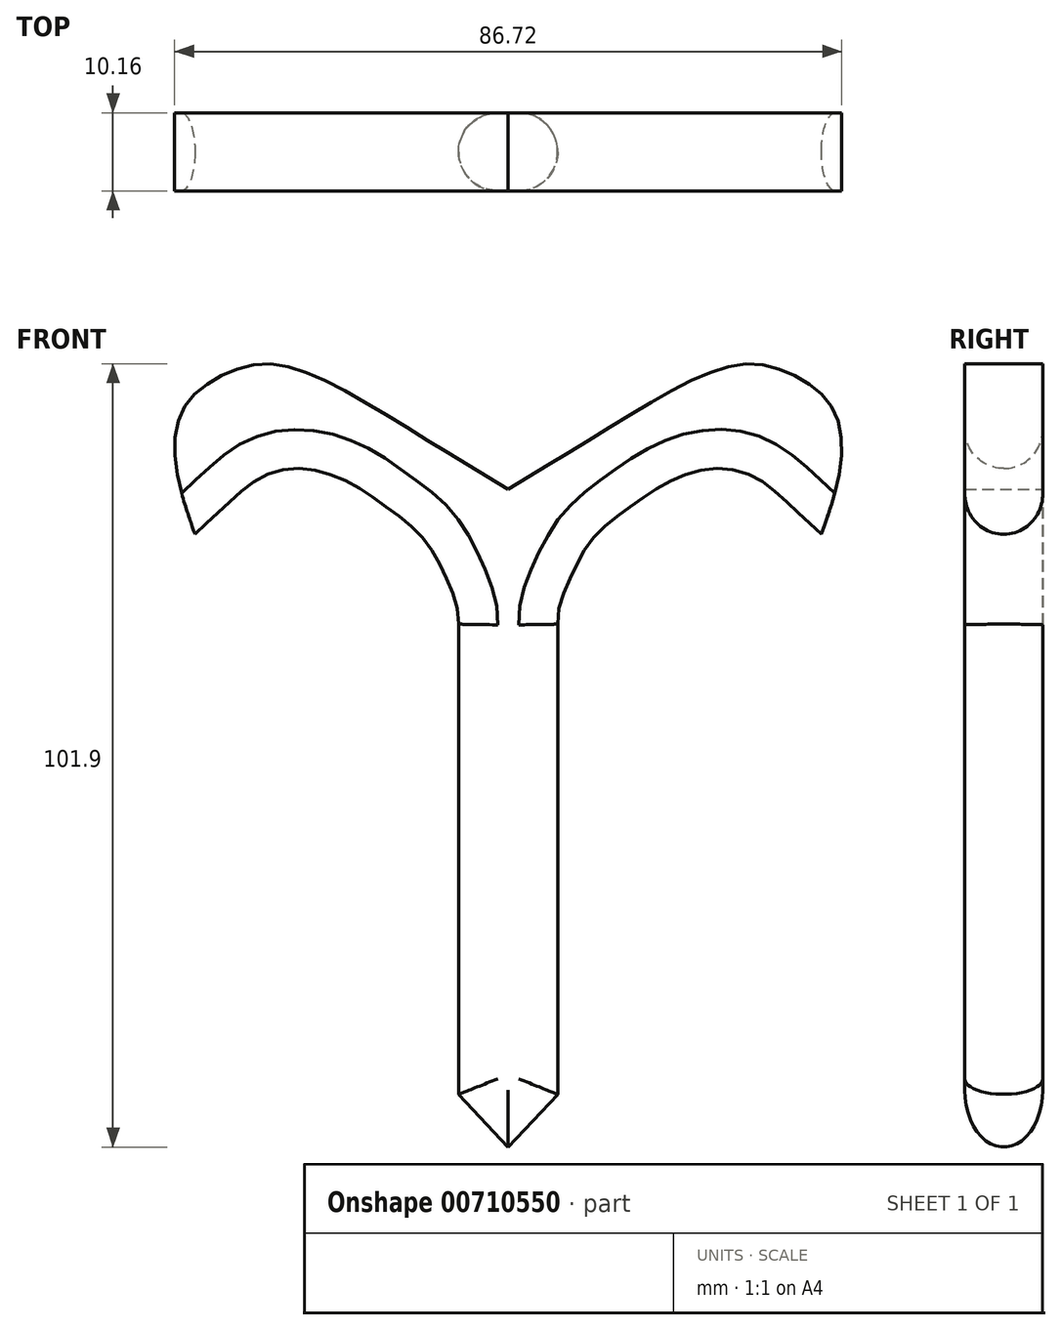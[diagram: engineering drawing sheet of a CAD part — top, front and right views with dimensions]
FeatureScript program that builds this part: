
annotation { "Feature Type Name" : "Feature", "Feature Type Description" : "" }
export const myFeature = defineFeature(function(context is Context, id is Id, definition is map)
    precondition{}
    {
        {
            var Q0;
            Q0=qCreatedBy(makeId("Front.planeOp"),FACE);
            var sketch = newSketch(context, id + "F0", { "sketchPlane" : qUnion([Q0])});
            skFitSpline(sketch, "E0", {"points": [v(-40.72, -3.3) * mm, v(-36.06, 1.06) * mm, v(-31.4, 4.47) * mm, v(-25.7, 5.13) * mm, v(-20, 3.06) * mm, v(-15.49, 0) * mm, v(-11.42, -3.38) * mm, v(-8.6, -7.82) * mm, v(-6.6, -12.85) * mm, v(-6.46, -15) * mm], "startDerivative": vector(37.94, 35.86) * mm, "endDerivative": vector(-0.94, -26.86) * mm});
            skLineSegment(sketch, "E1", {"start": v(-6.46, -15) * mm, "end": v(-6.46, -76.17) * mm});
            skLineSegment(sketch, "E2", {"start": v(-6.46, -76.17) * mm, "end": v(0, -83.02) * mm});
            skFitSpline(sketch, "E3", {"points": [v(-40.72, -3.3) * mm, v(-43.2, 5.6) * mm, v(-42.39, 12.7) * mm, v(-38.07, 16.9) * mm, v(-31.55, 18.88) * mm, v(-23.28, 16.43) * mm, v(-11.51, 9.56) * mm, v(0, 2.57) * mm], "startDerivative": vector(-21.78, 62.02) * mm, "endDerivative": vector(65.3, -39.32) * mm});
            skLineSegment(sketch, "E4", {"start": v(0, -5.7) * mm, "end": v(0, -12.11) * mm});
            skFitSpline(sketch, "E5.MirrorCS", {"points": [v(40.72, -3.3) * mm, v(43.2, 5.6) * mm, v(42.39, 12.7) * mm, v(38.07, 16.9) * mm, v(31.55, 18.88) * mm, v(23.28, 16.43) * mm, v(11.51, 9.56) * mm, v(0, 2.57) * mm], "startDerivative": vector(21.78, 62.02) * mm, "endDerivative": vector(-65.3, -39.32) * mm});
            skFitSpline(sketch, "E6.MirrorCS", {"points": [v(40.72, -3.3) * mm, v(36.06, 1.06) * mm, v(31.4, 4.47) * mm, v(25.7, 5.13) * mm, v(20, 3.06) * mm, v(15.49, 0) * mm, v(11.42, -3.38) * mm, v(8.6, -7.82) * mm, v(6.6, -12.85) * mm, v(6.46, -15) * mm], "startDerivative": vector(-37.94, 35.86) * mm, "endDerivative": vector(0.94, -26.86) * mm});
            skLineSegment(sketch, "E7.MirrorCS", {"start": v(6.46, -15) * mm, "end": v(6.46, -76.17) * mm});
            skLineSegment(sketch, "E8.MirrorCS", {"start": v(6.46, -76.17) * mm, "end": v(0, -83.02) * mm});
            skSolve(sketch);
        }
        {
            var Q0;
            Q0=makeQuery(id+"F0.imprint","IMPRINT",FACE,{"disambiguationData":[TD([[makeQuery(id+"F0.imprint","IMPRINT",EDGE,{"derivedFrom":sQuery(id+"F0.wireOp",EDGE,"E0")}),1.0]])]});
            extrude(context, id + "F1", {"entities" : qUnion([Q0]), "depth" : 5.08 * mm, "offsetDistance" : 25.4 * mm});
        }
        {
            var Q0;
            Q0=makeQuery(id+"F1.opExtrude","CAP_FACE",FACE,{"disambiguationData":[OSD([sQuery(id+"F0.wireOp",EDGE,"E0"),sQuery(id+"F0.wireOp",EDGE,"E1"),sQuery(id+"F0.wireOp",EDGE,"E2"),sQuery(id+"F0.wireOp",EDGE,"E3"),sQuery(id+"F0.wireOp",EDGE,"E5.MirrorCS"),sQuery(id+"F0.wireOp",EDGE,"E6.MirrorCS"),sQuery(id+"F0.wireOp",EDGE,"E7.MirrorCS"),sQuery(id+"F0.wireOp",EDGE,"E8.MirrorCS")])],"isStart":true});
            extrude(context, id + "F2", {"entities" : qUnion([Q0]), "operationType" : NewBodyOperationType.ADD, "depth" : 5.08 * mm, "offsetDistance" : 25.4 * mm});
        }
        {
            var Q0;
            Q0=makeQuery(id+"F2.opExtrude","CAP_EDGE",EDGE,{"disambiguationData":[OSD([sQuery(id+"F0.wireOp",EDGE,"E0")])],"isStart":false});
            var Q1;
            Q1=makeQuery(id+"F2.opExtrude","CAP_EDGE",EDGE,{"disambiguationData":[OSD([sQuery(id+"F0.wireOp",EDGE,"E6.MirrorCS")])],"isStart":false});
            var Q2;
            Q2=makeQuery(id+"F2.opExtrude","CAP_EDGE",EDGE,{"disambiguationData":[OSD([sQuery(id+"F0.wireOp",EDGE,"E8.MirrorCS")])],"isStart":false});
            var Q3;
            Q3=makeQuery(id+"F2.opExtrude","CAP_EDGE",EDGE,{"disambiguationData":[OSD([sQuery(id+"F0.wireOp",EDGE,"E2")])],"isStart":false});
            var Q4;
            Q4=makeQuery(id+"F1.opExtrude","CAP_EDGE",EDGE,{"disambiguationData":[OSD([sQuery(id+"F0.wireOp",EDGE,"E8.MirrorCS")])],"isStart":false});
            var Q5;
            Q5=makeQuery(id+"F1.opExtrude","CAP_EDGE",EDGE,{"disambiguationData":[OSD([sQuery(id+"F0.wireOp",EDGE,"E2")])],"isStart":false});
            var Q6;
            Q6=makeQuery(id+"F1.opExtrude","CAP_EDGE",EDGE,{"disambiguationData":[OSD([sQuery(id+"F0.wireOp",EDGE,"E6.MirrorCS")])],"isStart":false});
            var Q7;
            Q7=makeQuery(id+"F1.opExtrude","CAP_EDGE",EDGE,{"disambiguationData":[OSD([sQuery(id+"F0.wireOp",EDGE,"E0")])],"isStart":false});
            fillet(context, id + "F3", {"entities" : qUnion([Q0, Q1, Q2, Q3, Q4, Q5, Q6, Q7]), "radius" : 5.08 * mm, "tangentPropagation" : true, "allowEdgeOverflow" : false});
        }
    });
